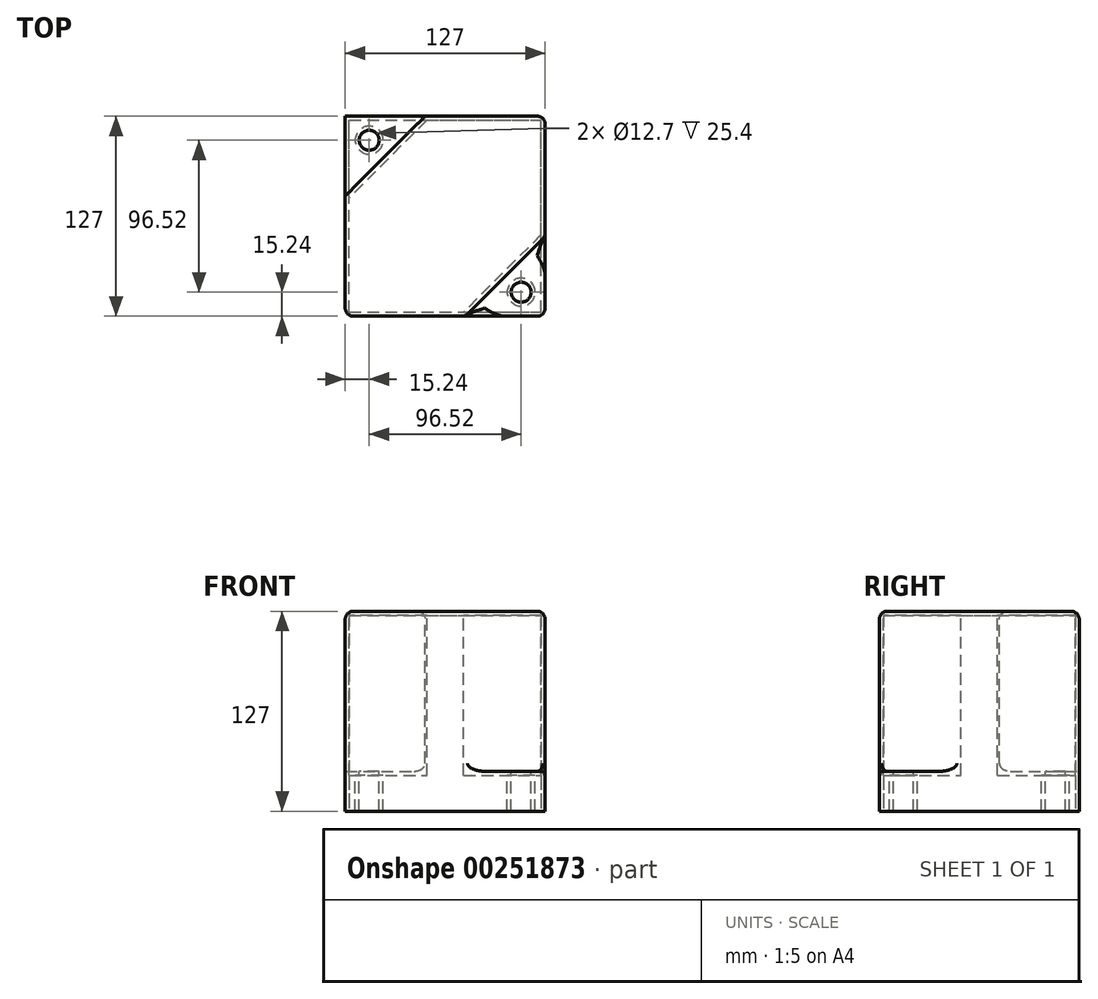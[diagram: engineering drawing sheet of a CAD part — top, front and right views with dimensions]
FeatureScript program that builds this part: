
annotation { "Feature Type Name" : "Feature", "Feature Type Description" : "" }
export const myFeature = defineFeature(function(context is Context, id is Id, definition is map)
    precondition{}
    {
        {
            var Q0;
            Q0=qCreatedBy(makeId("Front.planeOp"),FACE);
            var sketch = newSketch(context, id + "F0", { "sketchPlane" : qUnion([Q0])});
            skLineSegment(sketch, "E0.bottom", {"start": v(-63.5, 63.5) * mm, "end": v(63.5, 63.5) * mm});
            skLineSegment(sketch, "E0.top", {"start": v(-63.5, -63.5) * mm, "end": v(63.5, -63.5) * mm});
            skLineSegment(sketch, "E0.left", {"start": v(-63.5, 63.5) * mm, "end": v(-63.5, -63.5) * mm});
            skLineSegment(sketch, "E0.right", {"start": v(63.5, 63.5) * mm, "end": v(63.5, -63.5) * mm});
            skPoint(sketch, "E0.middle", {"position": v(0, 0) * mm});
            skSolve(sketch);
        }
        {
            var Q0;
            Q0 = qSketchRegion(id + "F0", true);
            extrude(context, id + "F1", {"entities" : qUnion([Q0]), "depth" : 127 * mm});
        }
        {
            var Q0;
            Q0=makeQuery(id+"F1.opExtrude","SWEPT_FACE",FACE,{"disambiguationData":[OSD([sQuery(id+"F0.wireOp",EDGE,"E0.bottom")])]});
            var sketch = newSketch(context, id + "F2", { "sketchPlane" : qUnion([Q0])});
            skLineSegment(sketch, "E1", {"start": v(-63.5, 0) * mm, "end": v(-12.7, 0) * mm});
            skLineSegment(sketch, "E2", {"start": v(-12.7, 0) * mm, "end": v(-63.5, -50.8) * mm});
            skLineSegment(sketch, "E3", {"start": v(-63.5, -50.8) * mm, "end": v(-63.5, 0) * mm});
            skLineSegment(sketch, "E4", {"start": v(63.5, -127) * mm, "end": v(63.5, -76.2) * mm});
            skLineSegment(sketch, "E5", {"start": v(63.5, -76.2) * mm, "end": v(12.7, -127) * mm});
            skLineSegment(sketch, "E6", {"start": v(12.7, -127) * mm, "end": v(63.5, -127) * mm});
            skSolve(sketch);
        }
        {
            var Q0;
            Q0=makeQuery(id+"F2.imprint","IMPRINT",FACE,{"disambiguationData":[TD([[makeQuery(id+"F2.imprint","IMPRINT",EDGE,{"derivedFrom":sQuery(id+"F2.wireOp",EDGE,"E1")}),-1.0]])]});
            var Q1;
            Q1=makeQuery(id+"F2.imprint","IMPRINT",FACE,{"disambiguationData":[TD([[makeQuery(id+"F2.imprint","IMPRINT",EDGE,{"derivedFrom":sQuery(id+"F2.wireOp",EDGE,"E4")}),1.0]])]});
            extrude(context, id + "F3", {"entities" : qUnion([Q0, Q1]), "operationType" : NewBodyOperationType.REMOVE, "oppositeDirection" : true, "depth" : 101.6 * mm});
        }
        {
            var Q0;
            Q0=makeQuery(id+"F1.opExtrude","SWEPT_FACE",FACE,{"disambiguationData":[OSD([sQuery(id+"F0.wireOp",EDGE,"E0.bottom")])]});
            var sketch = newSketch(context, id + "F4", { "sketchPlane" : qUnion([Q0])});
            skCircle(sketch, "E7", {"center": v(-48.26, -15.24) * mm, "radius": 6.35 * mm});
            skCircle(sketch, "E8", {"center": v(48.26, -111.76) * mm, "radius": 6.35 * mm});
            skSolve(sketch);
        }
        {
            var Q0;
            Q0=makeQuery(id+"F4.imprint","IMPRINT",FACE,{"disambiguationData":[TD([[makeQuery(id+"F4.imprint","IMPRINT",EDGE,{"derivedFrom":sQuery(id+"F4.wireOp",EDGE,"E7")}),1.0]])]});
            var Q1;
            Q1=makeQuery(id+"F4.imprint","IMPRINT",FACE,{"disambiguationData":[TD([[makeQuery(id+"F4.imprint","IMPRINT",EDGE,{"derivedFrom":sQuery(id+"F4.wireOp",EDGE,"E8")}),1.0]])]});
            extrude(context, id + "F5", {"entities" : qUnion([Q0, Q1]), "operationType" : NewBodyOperationType.REMOVE, "oppositeDirection" : true, "depth" : 203.2 * mm});
        }
        {
            var Q0;
            Q0=makeQuery(id+"F1.opExtrude","SWEPT_FACE",FACE,{"disambiguationData":[OSD([sQuery(id+"F0.wireOp",EDGE,"E0.top")])]});
            shell(context, id + "F6", {"entities" : qUnion([Q0]), "thickness" : 2.54 * mm});
        }
        {
            var Q0;
            Q0=makeQuery(id+"F3.boolean.opBoolean","COPY",EDGE,{"derivedFrom":makeQuery(id+"F3.opExtrude","CAP_EDGE",EDGE,{"disambiguationData":[OSD([sQuery(id+"F2.wireOp",EDGE,"E2")])],"isStart":true})});
            var Q1;
            Q1=makeQuery(id+"F1.opExtrude","SWEPT_EDGE",EDGE,{"disambiguationData":[OSD([sQuery(id+"F0.wireOp",EDGE,"E0.bottom"),sQuery(id+"F0.wireOp",EDGE,"E0.left")])]});
            var Q2;
            Q2=makeQuery(id+"F3.boolean.opBoolean","COPY",EDGE,{"derivedFrom":makeQuery(id+"F3.opExtrude","SWEPT_EDGE",EDGE,{"disambiguationData":[OSD([sQuery(id+"F0.wireOp",EDGE,"E0.bottom"),sQuery(id+"F0.wireOp",EDGE,"E0.left"),sQuery(id+"F2.wireOp",EDGE,"E2"),sQuery(id+"F2.wireOp",EDGE,"E3")])]})});
            var Q3;
            Q3=makeQuery(id+"F3.boolean.opBoolean","COPY",EDGE,{"derivedFrom":makeQuery(id+"F3.opExtrude","SWEPT_EDGE",EDGE,{"disambiguationData":[OSD([sQuery(id+"F0.wireOp",EDGE,"E0.bottom"),sQuery(id+"F2.wireOp",EDGE,"E1"),sQuery(id+"F2.wireOp",EDGE,"E2")])]})});
            var Q4;
            Q4=makeQuery(id+"F1.opExtrude","CAP_EDGE",EDGE,{"disambiguationData":[OSD([sQuery(id+"F0.wireOp",EDGE,"E0.bottom")])],"isStart":true});
            var Q5;
            Q5=makeQuery(id+"F1.opExtrude","SWEPT_EDGE",EDGE,{"disambiguationData":[OSD([sQuery(id+"F0.wireOp",EDGE,"E0.bottom"),sQuery(id+"F0.wireOp",EDGE,"E0.right")])]});
            var Q6;
            Q6=makeQuery(id+"F3.boolean.opBoolean","COPY",EDGE,{"derivedFrom":makeQuery(id+"F3.opExtrude","CAP_EDGE",EDGE,{"disambiguationData":[OSD([sQuery(id+"F2.wireOp",EDGE,"E5")])],"isStart":true})});
            var Q7;
            Q7=makeQuery(id+"F1.opExtrude","CAP_EDGE",EDGE,{"disambiguationData":[OSD([sQuery(id+"F0.wireOp",EDGE,"E0.bottom")])],"isStart":false});
            var Q8;
            Q8=makeQuery(id+"F1.opExtrude","CAP_EDGE",EDGE,{"disambiguationData":[OSD([sQuery(id+"F0.wireOp",EDGE,"E0.left")])],"isStart":false});
            var Q9;
            Q9=makeQuery(id+"F3.boolean.opBoolean","COPY",FACE,{"derivedFrom":makeQuery(id+"F3.opExtrude","SWEPT_FACE",FACE,{"disambiguationData":[OSD([sQuery(id+"F2.wireOp",EDGE,"E5")])]})});
            var Q10;
            Q10=makeQuery(id+"F1.opExtrude","CAP_EDGE",EDGE,{"disambiguationData":[OSD([sQuery(id+"F0.wireOp",EDGE,"E0.right")])],"isStart":true});
            var Q11;
            Q11=makeQuery(id+"F1.opExtrude","CAP_EDGE",EDGE,{"disambiguationData":[OSD([sQuery(id+"F0.wireOp",EDGE,"E0.right")])],"isStart":false});
            var Q12;
            Q12=makeQuery(id+"F3.boolean.opBoolean","COPY",EDGE,{"derivedFrom":makeQuery(id+"F3.opExtrude","CAP_EDGE",EDGE,{"disambiguationData":[OSD([sQuery(id+"F2.wireOp",EDGE,"E1")])],"isStart":false})});
            var Q13;
            Q13=makeQuery(id+"F3.boolean.opBoolean","COPY",EDGE,{"derivedFrom":makeQuery(id+"F3.opExtrude","CAP_EDGE",EDGE,{"disambiguationData":[OSD([sQuery(id+"F2.wireOp",EDGE,"E3")])],"isStart":false})});
            var Q14;
            Q14=makeQuery(id+"F3.boolean.opBoolean","COPY",EDGE,{"derivedFrom":makeQuery(id+"F3.opExtrude","CAP_EDGE",EDGE,{"disambiguationData":[OSD([sQuery(id+"F2.wireOp",EDGE,"E2")])],"isStart":false})});
            fillet(context, id + "F7", {"entities" : qUnion([Q0, Q1, Q2, Q3, Q4, Q5, Q6, Q7, Q8, Q9, Q10, Q11, Q12, Q13, Q14]), "radius" : 5.08 * mm, "tangentPropagation" : true, "allowEdgeOverflow" : false});
        }
    });
